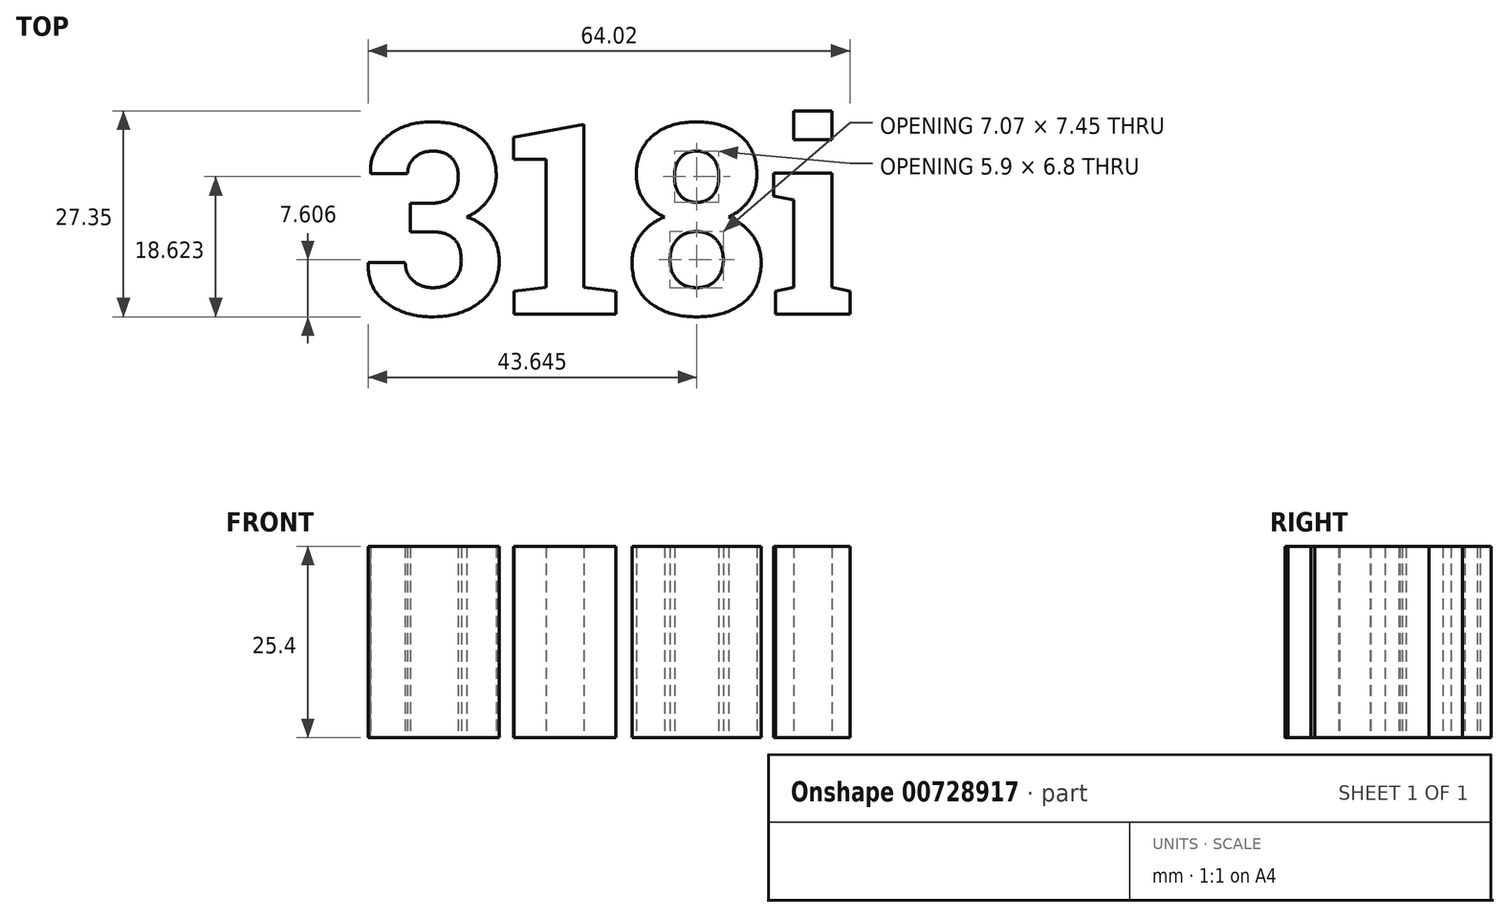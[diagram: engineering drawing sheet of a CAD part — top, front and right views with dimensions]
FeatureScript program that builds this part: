
annotation { "Feature Type Name" : "Feature", "Feature Type Description" : "" }
export const myFeature = defineFeature(function(context is Context, id is Id, definition is map)
    precondition{}
    {
        {
            var Q0;
            Q0=qCreatedBy(makeId("Top.planeOp"),FACE);
            var sketch = newSketch(context, id + "F0", { "sketchPlane" : qUnion([Q0])});
            skText(sketch, "E0", { "text": "318i", "fontName": "RobotoSlab-Bold.ttf"});
            const initialGuessF0  = {"E0": [-0.05185, 0.02626, 1, 0, 0.0255]};
            skSetInitialGuess(sketch, initialGuessF0);
            skSolve(sketch);
        }
        {
            var Q0;
            Q0 = qSketchRegion(id + "F0", true);
            extrude(context, id + "F1", {"entities" : qUnion([Q0]), "depth" : 25.4 * mm, "offsetDistance" : 25.4 * mm});
        }
    });
